FCSTD DOCUMENT  (FreeCAD 2022.430R26244 +4758 (Git))
Label: MonsterKossel_dimensions
License: All rights reserved
LicenseURL: http://en.wikipedia.org/wiki/All_rights_reserved
objects: Spreadsheet::Sheet×1

FEATURE [Spreadsheet::Sheet] Spreadsheet  label="Dimensions"
  PythonMode = false
  ShowCells = 0
  TreeRank = 1
  cells = A1=Bed Diameter; B1(bed_dia)==350mm; A2=Printable square; B2(square_side)==sqrt(bed_dia ^ 2 / 2); A3=Max Print Height; B3(print_height)==440mm; A4=Minimum rod length; B4(rod_length)==450mm; A5=Panel Height; B5(panel_height)==beam_height - 100; A6=Vertical Extrusion Length; B6(beam_height)==1000mm; A7=Horizontal Extrusion Length; B7(beam_width)==567.47mm; A8=Effector Diameter; B8(effector_dia)==60mm; A9=Hotend Height (below effector); B9(hotend_height)==65mm; A10=Rail length; B10(rail_length)==700mm; A11=Belt Length; B11(belt_length)==1900mm; A12=Bed Thickness; B12(bed_thickness)==6mm; A13=Bed mounting hole spacing; B13(bed_hole_spacing)==60mm; A14=Panel width; B14(panel_width)==beam_width + 2 * 29.78mm; A15=Panel thickness; B15(panel_thickness)==3mm; A16=Telescoping square tube outer size; B16(tube_outer_side)==15.5mm; A17=Telescoping tube middle size; B17(tube_middle_size)==11.5mm; A18=Telescoping tube inner size; B18(tube_inner_size)==7.5mm; A19=Telescoping tube segment length; B19(shaft_segment_length)==300mm; A20=Telescoping tube minimum length; A21=Telescoping tube maximum length; A22=U joint inner diameter; B22(ujoint_id)==4mm; A23=Needle bearing OD; B23(needle_bearing_OD)==7mm; A24=Needle bearing length; B24(needle_bearing_length)==7mm; A25=Ujoint bearing OD; B25(bearing_od)==8mm; A26=Ujoint bearing thickness; B26(bearing_thickness)==3mm
